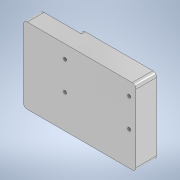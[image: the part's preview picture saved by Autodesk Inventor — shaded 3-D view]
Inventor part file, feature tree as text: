
AUTODESK INVENTOR PART (.ipt)
format: ipt  version: 2021 (Build 250183000, 183)  size: 131,072 bytes
history: native  units: mm
features: reference x4, extrude x3, sketch x3, fillet x2, other x1
ambient origin geometry x8: Origin, YZ Plane, XZ Plane, XY Plane, X Axis, Y Axis, Z Axis, Center Point
bodies: Solid1 (feature_tree)
feature tree (13):
  extrude  "Extrusion1"  Depth=58.7mm
  extrude  "Extrusion2"  Depth=10.75mm
  extrude  "Extrusion3"  Depth=2.0mm
  fillet  "Fillet1"  Radius=1.6mm
  fillet  "Fillet2"  [1 undecoded]
  sketch  "Sketch1"  dims[d0=39.4mm d1=58.7mm]
  sketch  "Sketch2"  dims[d2=10.75mm d3=0.0mm d4=1.6mm]
  reference  "Reference1"
  reference  "Reference2"
  reference  "Reference3"
  reference  "Reference4"
  sketch  "Sketch5"  dims[d5=1.6mm d6=1.6mm d7=1.6mm d8=0.0mm d9=0.0mm d10=19.55mm d11=2.0mm d12=0.0mm d13=2.0mm d14=2.0mm]
  other  "682-13450_PORG_ME_THER_ASSY.iam"
note: 1 required parameter value undecoded (feature->parameter linkage not recoverable at this tier; creation-order binding heuristic only, values carry confidence <= 0.55)
